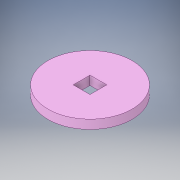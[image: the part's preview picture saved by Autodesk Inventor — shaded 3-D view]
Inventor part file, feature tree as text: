
AUTODESK INVENTOR PART (.ipt)
format: ipt  version: 2019 (Build 230136000, 136)  size: 111,616 bytes
history: native  units: mm
features: other x1, extrude x1, sketch x1
ambient origin geometry x8: Origin, YZ Plane, XZ Plane, XY Plane, X Axis, Y Axis, Z Axis, Center Point
bodies: Body1 (feature_tree)
feature tree (3):
  other  "Sólido1"
  extrude  "Extrusión1"  Depth=6.0mm
  sketch  "Boceto1"  dims[d0=6.0mm d1=6.0mm d2=30.0mm d3=3.18mm d4=0.0mm]
